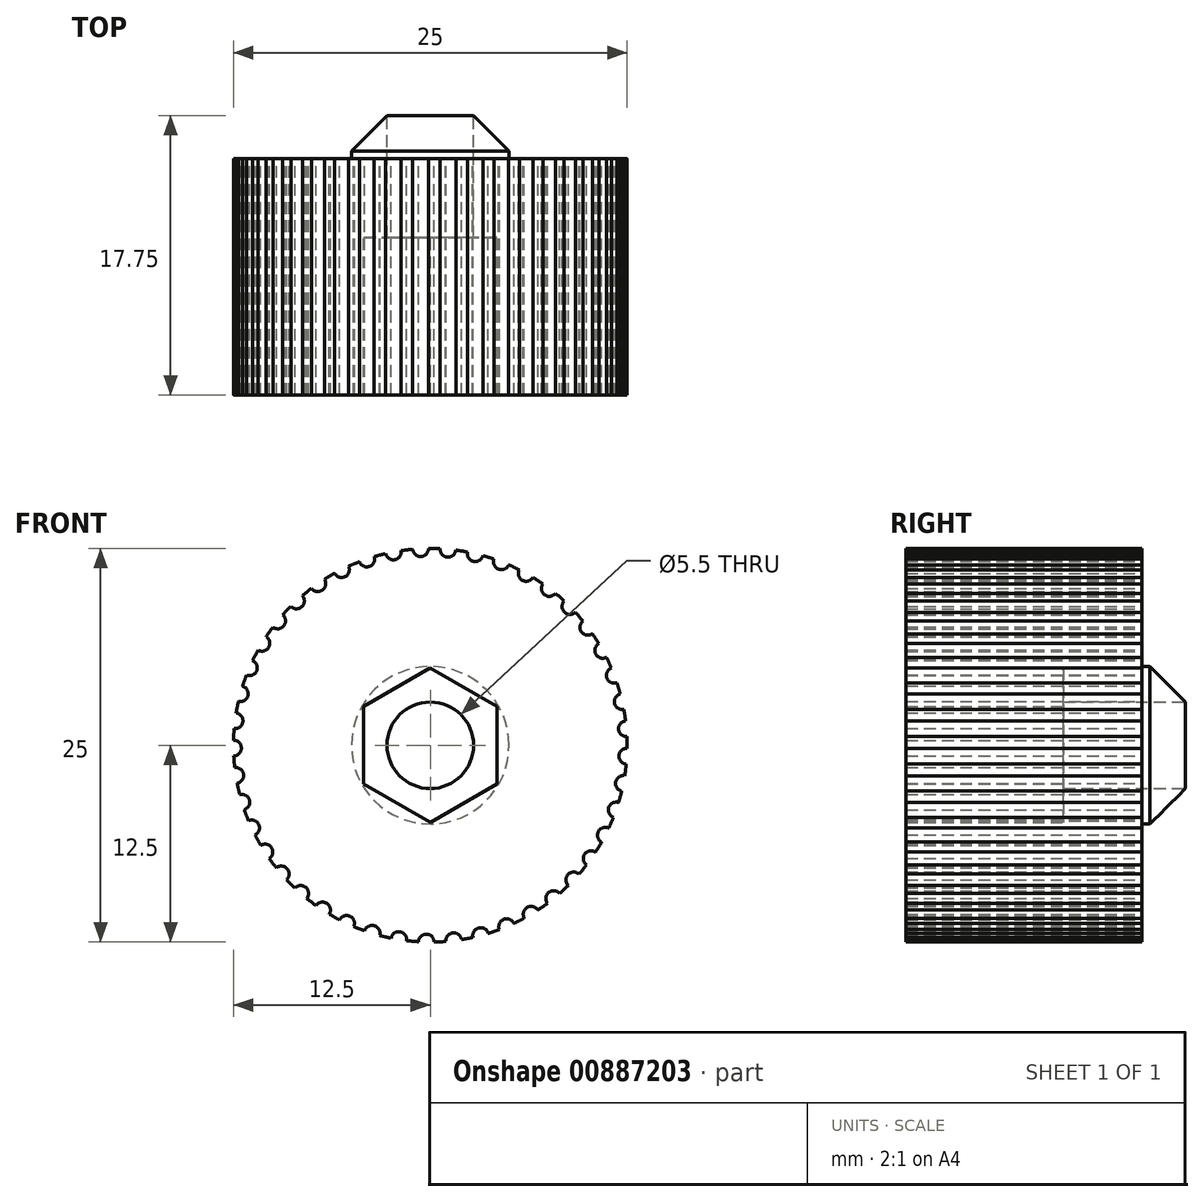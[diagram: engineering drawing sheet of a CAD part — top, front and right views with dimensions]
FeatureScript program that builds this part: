
annotation { "Feature Type Name" : "Feature", "Feature Type Description" : "" }
export const myFeature = defineFeature(function(context is Context, id is Id, definition is map)
    precondition{}
    {
        {
            var Q0;
            Q0=qCreatedBy(makeId("Front.planeOp"),FACE);
            var sketch = newSketch(context, id + "F0", { "sketchPlane" : qUnion([Q0])});
            skCircle(sketch, "E0.cCircle", {"center": v(0, 0) * mm, "radius": 4.25 * mm, "construction": true});
            skLineSegment(sketch, "E0.0", {"start": v(-4.25, 2.45) * mm, "end": v(0, 4.9) * mm});
            skLineSegment(sketch, "E0.1", {"start": v(0, 4.9) * mm, "end": v(4.25, 2.46) * mm});
            skLineSegment(sketch, "E0.2", {"start": v(4.25, 2.46) * mm, "end": v(4.25, -2.45) * mm});
            skLineSegment(sketch, "E0.3", {"start": v(4.25, -2.45) * mm, "end": v(0, -4.9) * mm});
            skLineSegment(sketch, "E0.4", {"start": v(0, -4.9) * mm, "end": v(-4.25, -2.46) * mm});
            skLineSegment(sketch, "E0.5", {"start": v(-4.25, -2.46) * mm, "end": v(-4.25, 2.45) * mm});
            skPoint(sketch, "E0.0.midPoint", {"position": v(-2.13, 3.68) * mm});
            skCircle(sketch, "E1", {"center": v(0, 0) * mm, "radius": 2.75 * mm});
            skCircle(sketch, "E2", {"center": v(0, 0) * mm, "radius": 12.5 * mm});
            skCircle(sketch, "E3", {"center": v(0, 0) * mm, "radius": 5 * mm});
            skSolve(sketch);
        }
        {
            var Q0;
            Q0=makeQuery(id+"F0.imprint","IMPRINT",FACE,{"disambiguationData":[TD([[makeQuery(id+"F0.imprint","IMPRINT",EDGE,{"derivedFrom":sQuery(id+"F0.wireOp",EDGE,"E2")}),1.0]])]});
            extrude(context, id + "F1", {"entities" : qUnion([Q0]), "depth" : 15 * mm, "offsetDistance" : 25 * mm});
        }
        {
            var Q0;
            Q0=makeQuery(id+"F0.imprint","IMPRINT",FACE,{"disambiguationData":[TD([[makeQuery(id+"F0.imprint","IMPRINT",EDGE,{"derivedFrom":sQuery(id+"F0.wireOp",EDGE,"E0.0")}),1.0]])]});
            extrude(context, id + "F2", {"entities" : qUnion([Q0]), "operationType" : NewBodyOperationType.ADD, "depth" : 15 * mm, "offsetDistance" : 25 * mm});
        }
        {
            var Q0;
            Q0=makeQuery(id+"F0.imprint","IMPRINT",FACE,{"disambiguationData":[TD([[makeQuery(id+"F0.imprint","IMPRINT",EDGE,{"derivedFrom":sQuery(id+"F0.wireOp",EDGE,"E0.0")}),-1.0]])]});
            extrude(context, id + "F3", {"entities" : qUnion([Q0]), "operationType" : NewBodyOperationType.ADD, "depth" : 5 * mm, "offsetDistance" : 25 * mm});
        }
        {
            var Q0;
            Q0=makeQuery(id+"F0.imprint","IMPRINT",FACE,{"disambiguationData":[TD([[makeQuery(id+"F0.imprint","IMPRINT",EDGE,{"derivedFrom":sQuery(id+"F0.wireOp",EDGE,"E0.0")}),1.0]])]});
            extrude(context, id + "F4", {"entities" : qUnion([Q0]), "operationType" : NewBodyOperationType.ADD, "oppositeDirection" : true, "depth" : 3 * mm, "offsetDistance" : 25 * mm});
        }
        {
            var Q0;
            Q0=makeQuery(id+"F0.imprint","IMPRINT",FACE,{"disambiguationData":[TD([[makeQuery(id+"F0.imprint","IMPRINT",EDGE,{"derivedFrom":sQuery(id+"F0.wireOp",EDGE,"E0.0")}),-1.0]])]});
            extrude(context, id + "F5", {"entities" : qUnion([Q0]), "operationType" : NewBodyOperationType.ADD, "oppositeDirection" : true, "depth" : 3 * mm, "offsetDistance" : 25 * mm});
        }
        {
            var Q0;
            Q0=makeQuery(id+"F4.opExtrude","CAP_EDGE",EDGE,{"disambiguationData":[OSD([sQuery(id+"F0.wireOp",EDGE,"E3")])],"isStart":false});
            chamfer(context, id + "F6", {"entities" : qUnion([Q0]), "width" : 2.5 * mm, "tangentPropagation" : true});
        }
        {
            var Q0;
            Q0=qCreatedBy(makeId("Front.planeOp"),FACE);
            var sketch = newSketch(context, id + "F7", { "sketchPlane" : qUnion([Q0])});
            skCircle(sketch, "E4", {"center": v(-5.32, -11.31) * mm, "radius": 0.5 * mm});
            skCircle(sketch, "E5.1.0", {"center": v(-3.7, -11.94) * mm, "radius": 0.5 * mm});
            skCircle(sketch, "E5.2.0", {"center": v(-2, -12.34) * mm, "radius": 0.5 * mm});
            skCircle(sketch, "E5.3.0", {"center": v(-0.26, -12.5) * mm, "radius": 0.5 * mm});
            skCircle(sketch, "E5.4.0", {"center": v(1.48, -12.41) * mm, "radius": 0.5 * mm});
            skCircle(sketch, "E5.5.0", {"center": v(3.2, -12.08) * mm, "radius": 0.5 * mm});
            skCircle(sketch, "E5.6.0", {"center": v(4.85, -11.52) * mm, "radius": 0.5 * mm});
            skCircle(sketch, "E5.7.0", {"center": v(6.4, -10.73) * mm, "radius": 0.5 * mm});
            skCircle(sketch, "E5.8.0", {"center": v(7.84, -9.74) * mm, "radius": 0.5 * mm});
            skCircle(sketch, "E5.9.0", {"center": v(9.12, -8.55) * mm, "radius": 0.5 * mm});
            skCircle(sketch, "E5.10.0", {"center": v(10.22, -7.2) * mm, "radius": 0.5 * mm});
            skCircle(sketch, "E5.11.0", {"center": v(11.12, -5.7) * mm, "radius": 0.5 * mm});
            skCircle(sketch, "E5.12.0", {"center": v(11.8, -4.1) * mm, "radius": 0.5 * mm});
            skCircle(sketch, "E5.13.0", {"center": v(12.26, -2.42) * mm, "radius": 0.5 * mm});
            skCircle(sketch, "E5.14.0", {"center": v(12.48, -0.7) * mm, "radius": 0.5 * mm});
            skCircle(sketch, "E5.15.0", {"center": v(12.46, 1.05) * mm, "radius": 0.5 * mm});
            skCircle(sketch, "E5.16.0", {"center": v(12.19, 2.77) * mm, "radius": 0.5 * mm});
            skCircle(sketch, "E5.17.0", {"center": v(11.68, 4.44) * mm, "radius": 0.5 * mm});
            skCircle(sketch, "E5.18.0", {"center": v(10.95, 6.03) * mm, "radius": 0.5 * mm});
            skCircle(sketch, "E5.19.0", {"center": v(10, 7.5) * mm, "radius": 0.5 * mm});
            skCircle(sketch, "E5.20.0", {"center": v(8.87, 8.81) * mm, "radius": 0.5 * mm});
            skCircle(sketch, "E5.21.0", {"center": v(7.55, 9.96) * mm, "radius": 0.5 * mm});
            skCircle(sketch, "E5.22.0", {"center": v(6.1, 10.91) * mm, "radius": 0.5 * mm});
            skCircle(sketch, "E5.23.0", {"center": v(4.52, 11.66) * mm, "radius": 0.5 * mm});
            skCircle(sketch, "E5.24.0", {"center": v(2.85, 12.17) * mm, "radius": 0.5 * mm});
            skCircle(sketch, "E5.25.0", {"center": v(1.13, 12.45) * mm, "radius": 0.5 * mm});
            skCircle(sketch, "E5.26.0", {"center": v(-0.61, 12.48) * mm, "radius": 0.5 * mm});
            skCircle(sketch, "E5.27.0", {"center": v(-2.35, 12.28) * mm, "radius": 0.5 * mm});
            skCircle(sketch, "E5.28.0", {"center": v(-4.03, 11.83) * mm, "radius": 0.5 * mm});
            skCircle(sketch, "E5.29.0", {"center": v(-5.64, 11.16) * mm, "radius": 0.5 * mm});
            skCircle(sketch, "E5.30.0", {"center": v(-7.14, 10.26) * mm, "radius": 0.5 * mm});
            skCircle(sketch, "E5.31.0", {"center": v(-8.5, 9.17) * mm, "radius": 0.5 * mm});
            skCircle(sketch, "E5.32.0", {"center": v(-9.69, 7.9) * mm, "radius": 0.5 * mm});
            skCircle(sketch, "E5.33.0", {"center": v(-10.7, 6.47) * mm, "radius": 0.5 * mm});
            skCircle(sketch, "E5.34.0", {"center": v(-11.5, 4.92) * mm, "radius": 0.5 * mm});
            skCircle(sketch, "E5.35.0", {"center": v(-12.06, 3.27) * mm, "radius": 0.5 * mm});
            skCircle(sketch, "E5.36.0", {"center": v(-12.4, 1.56) * mm, "radius": 0.5 * mm});
            skCircle(sketch, "E5.37.0", {"center": v(-12.5, -0.18) * mm, "radius": 0.5 * mm});
            skCircle(sketch, "E5.38.0", {"center": v(-12.35, -1.92) * mm, "radius": 0.5 * mm});
            skCircle(sketch, "E5.39.0", {"center": v(-11.97, -3.62) * mm, "radius": 0.5 * mm});
            skCircle(sketch, "E5.40.0", {"center": v(-11.35, -5.25) * mm, "radius": 0.5 * mm});
            skCircle(sketch, "E5.41.0", {"center": v(-10.5, -6.77) * mm, "radius": 0.5 * mm});
            skCircle(sketch, "E5.42.0", {"center": v(-9.46, -8.17) * mm, "radius": 0.5 * mm});
            skCircle(sketch, "E5.43.0", {"center": v(-8.23, -9.4) * mm, "radius": 0.5 * mm});
            skCircle(sketch, "E5.44.0", {"center": v(-6.84, -10.46) * mm, "radius": 0.5 * mm});
            skPoint(sketch, "E5.center", {"position": v(0, 0) * mm});
            skSolve(sketch);
        }
        {
            var Q0;
            Q0=qSketchRegion(id+"F7",true);
            extrude(context, id + "F8", {"entities" : qUnion([Q0]), "operationType" : NewBodyOperationType.REMOVE, "depth" : 15 * mm, "offsetDistance" : 25 * mm});
        }
    });
